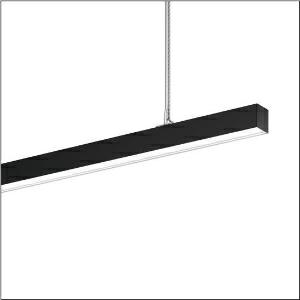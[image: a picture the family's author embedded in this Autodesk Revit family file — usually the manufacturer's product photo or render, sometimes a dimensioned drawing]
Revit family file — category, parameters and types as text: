
# Revit family: silica_r__21_51mx33tat7b_231b
name_source: partatom
category: Lighting Fixtures
units: mm (PartAtom-declared; Revit-internal decimal feet)

## family parameters
Cut with Voids When Loaded = No
Host = Face
Light Source = No
Part Type = Normal
Room Calculation Point = No
Round Connector Dimension = Use Diameter
Shared = No

## types (1)
- --- (1 x LED, 5740 lm, 53.8 W, 6500K)
    Apparent Load = 54 VA
    CIE Flux Codes = 78 96 99 56 100
    Color Rendering = 80
    Color Temperature = 6500K
    Default Elevation = 1800 mm
    Description = Silica® 21, office luminaire, primary optical cover: prismatic diffuser, of PMMA, CAT 2 (L<= 3000cd/m²), light emission: direct/indirect distribution, primary light characteristic: symmetric, installation type: suspended mounting, LED, rated luminous flux: 5.740lm, luminous efficacy: 102lm/W, light colour: 8tw, colour temperature: 2700..6500K, control gear: ECG DALI, with terminal, 3+2-pole, max. 2.5mm², mains connection: 220..240V, AC, 50/60Hz, rated input power: 56.5W, luminaire housing, of aluminium, jet black (RAL 9005), length: 1.204mm, width: 53mm, height: 53mm, protection rating (complete): IP20, insulation class (complete): insulation class I (protective earthing), certification: CE, permissible operating ambient temperature: 0..+35°C, standard: EN 50419, packaging unit: 1 piece
    Height = 53 mm
    Lamp = 1 x LED
    Lamp Light Flux = 5740 lm
    Lamp Power = 53.8 W
    Lamp count = 1
    Length = 1204 mm
    Luminous efficacy = 107 lm/W
    Manufacturer = Siteco
    ModVariant = No
    Model = 51MX33TAT7B
    Mounting Place = Ceiling
    Mounting Type = Pendant
    Number of Poles = 1
    OnlyDefault = Yes
    Power Factor = 1
    Product Name = Silica® 21
    Product group = office luminaire | ceiling pendant
    ProductGroupID = 902
    Protection Class = Protection class I
    Protection Degree = IP 20
    RLX_Detail_Level = 1
    RLX_Emergency_Light_Flux = 0 lm
    RLX_Emergency_Type = 0
    RLX_Emergency_Type_DB = No
    RlxData = <blob elided: 22909 chars, md5=574c2ccb>
    Socket = socket
    Standby Power = 0 W
    System Light Flux = 5740 lm
    System Power = 54 W
    Type Comments = individual setting
    Type Image = l_1297744.jpg
    URL = http://relux.com
    VarID = @adj_071089
    Voltage = 0 V
    Weight = 0.00 kg
    Width = 53 mm

## geometry (parser evidence)
native form markers: Blend x4, Sweep x13
no freeform markers — native parametric forms only
